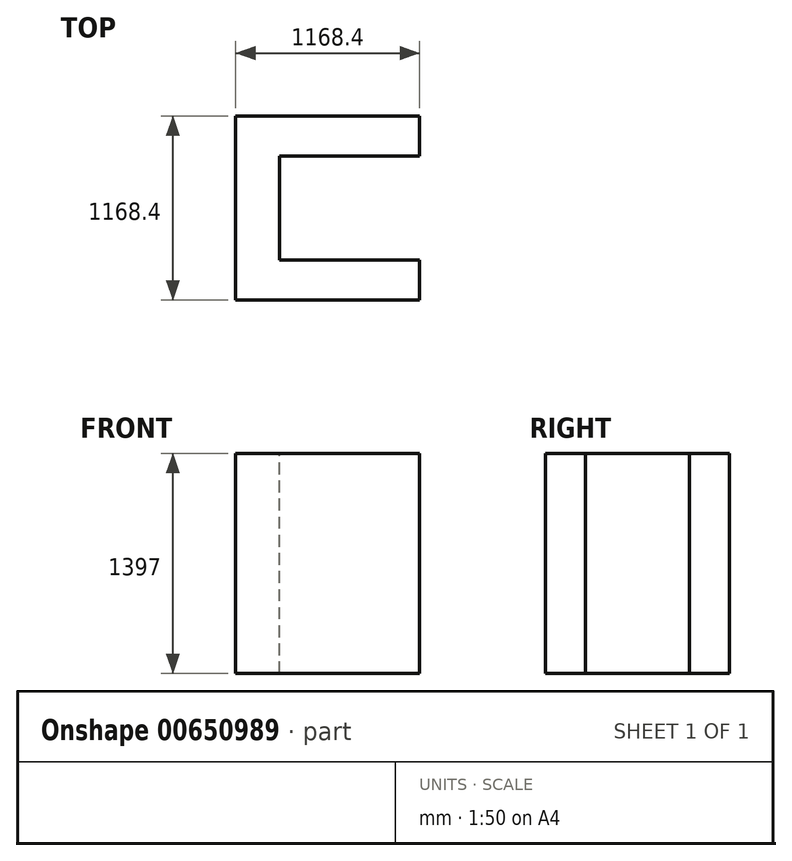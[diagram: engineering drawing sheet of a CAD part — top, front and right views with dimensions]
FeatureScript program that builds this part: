
annotation { "Feature Type Name" : "Feature", "Feature Type Description" : "" }
export const myFeature = defineFeature(function(context is Context, id is Id, definition is map)
    precondition{}
    {
        {
            var Q0;
            Q0=qCreatedBy(makeId("Right.planeOp"),FACE);
            var sketch = newSketch(context, id + "F0", { "sketchPlane" : qUnion([Q0])});
            skLineSegment(sketch, "E0.bottom", {"start": v(584.2, -698.5) * mm, "end": v(-584.2, -698.5) * mm});
            skLineSegment(sketch, "E0.top", {"start": v(584.2, 698.5) * mm, "end": v(-584.2, 698.5) * mm});
            skLineSegment(sketch, "E0.left", {"start": v(584.2, -698.5) * mm, "end": v(584.2, 698.5) * mm});
            skLineSegment(sketch, "E0.right", {"start": v(-584.2, -698.5) * mm, "end": v(-584.2, 698.5) * mm});
            skPoint(sketch, "E0.middle", {"position": v(0, 0) * mm});
            skSolve(sketch);
        }
        {
            var Q0;
            Q0=makeQuery(id+"F0.imprint","IMPRINT",FACE,{"disambiguationData":[TD([[makeQuery(id+"F0.imprint","IMPRINT",EDGE,{"derivedFrom":sQuery(id+"F0.wireOp",EDGE,"E0.bottom")}),-1.0]])]});
            extrude(context, id + "F1", {"entities" : qUnion([Q0]), "depth" : 279.4 * mm, "offsetDistance" : 25.4 * mm});
        }
        {
            var Q0;
            Q0=makeQuery(id+"F1.opExtrude","CAP_FACE",FACE,{"disambiguationData":[OSD([sQuery(id+"F0.wireOp",EDGE,"E0.bottom"),sQuery(id+"F0.wireOp",EDGE,"E0.top"),sQuery(id+"F0.wireOp",EDGE,"E0.left"),sQuery(id+"F0.wireOp",EDGE,"E0.right")])],"isStart":false});
            var sketch = newSketch(context, id + "F2", { "sketchPlane" : qUnion([Q0])});
            skLineSegment(sketch, "E1.bottom", {"start": v(-584.2, -698.5) * mm, "end": v(-330.2, -698.5) * mm});
            skLineSegment(sketch, "E1.top", {"start": v(-584.2, 698.5) * mm, "end": v(-330.2, 698.5) * mm});
            skLineSegment(sketch, "E1.left", {"start": v(-584.2, -698.5) * mm, "end": v(-584.2, 698.5) * mm});
            skLineSegment(sketch, "E1.right", {"start": v(-330.2, -698.5) * mm, "end": v(-330.2, 698.5) * mm});
            skLineSegment(sketch, "E2.bottom", {"start": v(584.2, -698.5) * mm, "end": v(330.2, -698.5) * mm});
            skLineSegment(sketch, "E2.top", {"start": v(584.2, 698.5) * mm, "end": v(330.2, 698.5) * mm});
            skLineSegment(sketch, "E2.left", {"start": v(584.2, -698.5) * mm, "end": v(584.2, 698.5) * mm});
            skLineSegment(sketch, "E2.right", {"start": v(330.2, -698.5) * mm, "end": v(330.2, 698.5) * mm});
            skSolve(sketch);
        }
        {
            var Q0;
            Q0=makeQuery(id+"F2.imprint","IMPRINT",FACE,{"disambiguationData":[TD([[makeQuery(id+"F2.imprint","IMPRINT",EDGE,{"derivedFrom":sQuery(id+"F2.wireOp",EDGE,"E1.bottom")}),-1.0]])]});
            var Q1;
            Q1=makeQuery(id+"F2.imprint","IMPRINT",FACE,{"disambiguationData":[TD([[makeQuery(id+"F2.imprint","IMPRINT",EDGE,{"derivedFrom":sQuery(id+"F2.wireOp",EDGE,"E2.bottom")}),-1.0]])]});
            extrude(context, id + "F3", {"entities" : qUnion([Q0, Q1]), "operationType" : NewBodyOperationType.ADD, "depth" : 889 * mm, "offsetDistance" : 25.4 * mm});
        }
    });
